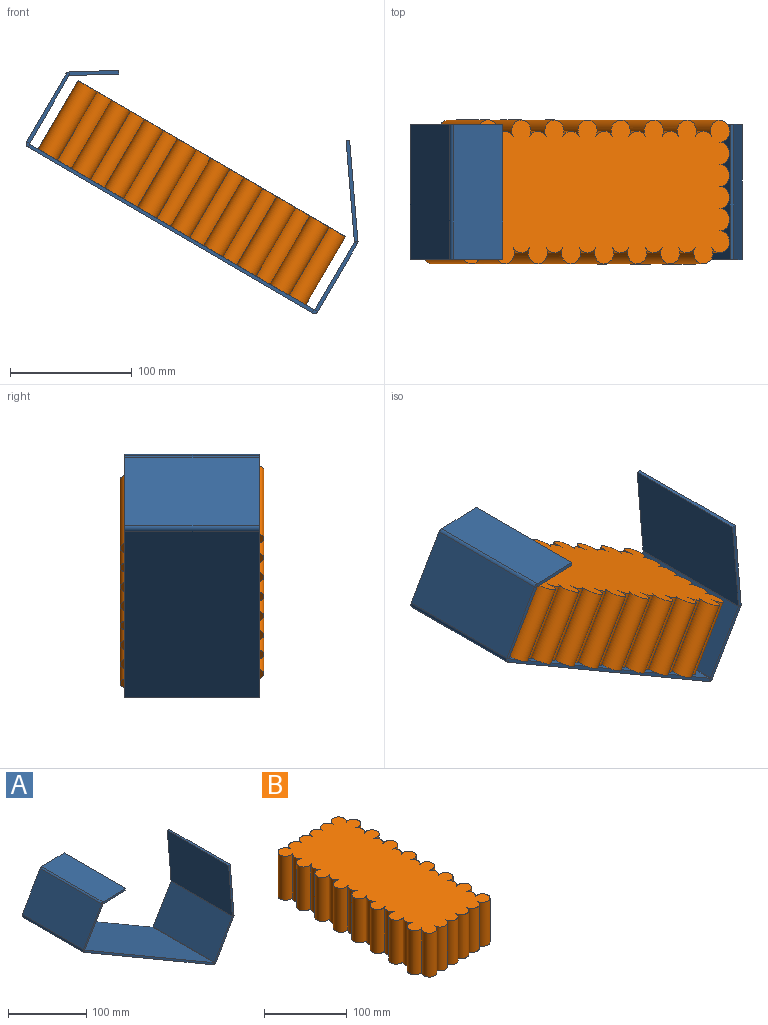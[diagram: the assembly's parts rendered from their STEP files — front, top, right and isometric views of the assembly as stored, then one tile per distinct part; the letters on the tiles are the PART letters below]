
ASSEMBLY  parts=2 mates=1
PART A: 38 faces, bbox 273x111x200 mm
  f0: plane 235.12x138.91mm, normal (0,-1,0), area 811.4mm2, adj f2,f3,f18,f35
  f1: plane 235.12x138.91mm, normal (0,1,0), area 811.4mm2, adj f2,f3,f17,f34
  f2: plane 233.6x136.32mm, normal (-0.5,0,-0.86), area 30022.3mm2, adj f0,f1,f19,f36
  f3: plane 233.6x136.32mm, normal (0.5,0,0.86), area 30022.3mm2, adj f0,f1,f20,f37
  f4: plane 40.59x4.22mm, normal (0,-1,0), area 121.5mm2, adj f5,f7,f8,f14
  f5: plane 111x3mm, normal (1,0,0.03), area 333mm2, adj f4,f6,f7,f8
  f6: plane 40.59x4.22mm, normal (0,1,0), area 121.5mm2, adj f5,f7,f8,f13
  f7: plane 111x40.5mm, normal (-0.03,0,1), area 4497.1mm2, adj f4,f5,f6,f15
  f8: plane 111x40.5mm, normal (0.03,0,-1), area 4497.1mm2, adj f4,f5,f6,f16
  f9: plane 56.98x34.96mm, normal (0,-1,0), area 192.7mm2, adj f11,f12,f14,f18
  f10: plane 56.98x34.96mm, normal (0,1,0), area 192.7mm2, adj f11,f12,f13,f17
  f11: plane 111x55.47mm, normal (-0.86,0,0.5), area 7128.7mm2, adj f9,f10,f15,f19
  f12: plane 111x55.47mm, normal (0.86,0,-0.5), area 7128.7mm2, adj f9,f10,f16,f20
  f13: plane 3.25x3.01mm, normal (0,1,0), area 6.1mm2, adj f6,f10,f15,f16
  f14: plane 3.25x3.01mm, normal (0,-1,0), area 6.1mm2, adj f4,f9,f15,f16
  f15: cylinder r=3.5mm len=111mm, axis (0,1,0), area 393.3mm2, adj f7,f11,f13,f14
  f16: cylinder r=0.5mm len=111mm, axis (0,1,0), area 56.2mm2, adj f8,f12,f13,f14
  f17: plane 4.79x3.25mm, normal (0,1,0), area 9.4mm2, adj f1,f10,f19,f20
  f18: plane 4.79x3.25mm, normal (0,-1,0), area 9.4mm2, adj f0,f9,f19,f20
  f19: cylinder r=3.5mm len=111mm, axis (0,1,0), area 610.3mm2, adj f2,f11,f17,f18
  f20: cylinder r=0.5mm len=111mm, axis (0,1,0), area 87.2mm2, adj f3,f12,f17,f18
  f21: plane 83.18x9.86mm, normal (0,-1,0), area 249.6mm2, adj f23,f24,f25,f31
  f22: plane 83.18x9.86mm, normal (0,1,0), area 249.6mm2, adj f23,f24,f25,f30
  f23: plane 111x2.99mm, normal (-0.08,0,1), area 333mm2, adj f21,f22,f24,f25
  f24: plane 111x82.93mm, normal (1,0,0.08), area 9236.9mm2, adj f21,f22,f23,f32
  f25: plane 111x82.93mm, normal (-1,0,-0.08), area 9236.9mm2, adj f21,f22,f23,f33
  f26: plane 57.08x35.02mm, normal (0,-1,0), area 193mm2, adj f28,f29,f31,f35
  f27: plane 57.08x35.02mm, normal (0,1,0), area 193mm2, adj f28,f29,f30,f34
  f28: plane 111x55.57mm, normal (0.86,0,-0.5), area 7142mm2, adj f26,f27,f32,f36
  f29: plane 111x55.57mm, normal (-0.86,0,0.5), area 7142mm2, adj f26,f27,f33,f37
  f30: plane 3.07x2.05mm, normal (0,1,0), area 3.7mm2, adj f22,f27,f32,f33
  f31: plane 3.07x2.05mm, normal (0,-1,0), area 3.7mm2, adj f21,f26,f32,f33
  f32: cylinder r=3.5mm len=111mm, axis (0,1,0), area 237.3mm2, adj f24,f28,f30,f31
  f33: cylinder r=0.5mm len=111mm, axis (0,1,0), area 33.9mm2, adj f25,f29,f30,f31
  f34: plane 4.79x3.25mm, normal (0,1,0), area 9.4mm2, adj f1,f27,f36,f37
  f35: plane 4.79x3.25mm, normal (0,-1,0), area 9.4mm2, adj f0,f26,f36,f37
  f36: cylinder r=3.5mm len=111mm, axis (0,1,0), area 610.3mm2, adj f2,f28,f34,f35
  f37: cylinder r=0.5mm len=111mm, axis (0,1,0), area 87.2mm2, adj f3,f29,f34,f35
PART B: 42 faces, bbox 118.3x254.6x65 mm
  f0: cylinder r=9.1mm len=65mm, axis (0,0,-1), area 2477.7mm2, adj f1,f39,f40,f41
  f1: cylinder r=9.1mm len=65mm, axis (0,0,-1), area 1858.3mm2, adj f0,f2,f40,f41
  f2: cylinder r=9.1mm len=65mm, axis (0,0,-1), area 1858.3mm2, adj f1,f3,f40,f41
  f3: cylinder r=9.1mm len=65mm, axis (0,0,-1), area 1858.3mm2, adj f2,f4,f40,f41
  f4: cylinder r=9.1mm len=65mm, axis (0,0,-1), area 1858.3mm2, adj f3,f5,f40,f41
  f5: cylinder r=9.1mm len=65mm, axis (0,0,-1), area 3097.1mm2, adj f4,f6,f40,f41
  f6: cylinder r=9.1mm len=65mm, axis (0,0,-1), area 1235.5mm2, adj f5,f7,f40,f41
  f7: cylinder r=9.1mm len=65mm, axis (0,0,-1), area 2474.4mm2, adj f6,f8,f40,f41
  f8: cylinder r=9.1mm len=65mm, axis (0,0,-1), area 1235.5mm2, adj f7,f9,f40,f41
  f9: cylinder r=9.1mm len=65mm, axis (0,0,-1), area 2474.4mm2, adj f8,f10,f40,f41
  f10: cylinder r=9.1mm len=65mm, axis (0,0,-1), area 1235.5mm2, adj f9,f11,f40,f41
  f11: cylinder r=9.1mm len=65mm, axis (0,0,-1), area 2474.4mm2, adj f10,f12,f40,f41
  f12: cylinder r=9.1mm len=65mm, axis (0,0,-1), area 1235.5mm2, adj f11,f13,f40,f41
  f13: cylinder r=9.1mm len=65mm, axis (0,0,-1), area 2474.4mm2, adj f12,f14,f40,f41
  f14: cylinder r=9.1mm len=65mm, axis (0,0,-1), area 1235.5mm2, adj f13,f15,f40,f41
  f15: cylinder r=9.1mm len=65mm, axis (0,0,-1), area 2474.4mm2, adj f14,f16,f40,f41
  f16: cylinder r=9.1mm len=65mm, axis (0,0,-1), area 1235.5mm2, adj f15,f17,f40,f41
  f17: cylinder r=9.1mm len=65mm, axis (0,0,-1), area 2474.4mm2, adj f16,f18,f40,f41
  f18: cylinder r=9.1mm len=65mm, axis (0,0,-1), area 1235.5mm2, adj f17,f19,f40,f41
  f19: cylinder r=9.1mm len=65mm, axis (0,0,-1), area 2474.4mm2, adj f18,f20,f40,f41
  f20: cylinder r=9.1mm len=65mm, axis (0,0,-1), area 2477.7mm2, adj f19,f21,f40,f41
  f21: cylinder r=9.1mm len=65mm, axis (0,0,-1), area 1858.3mm2, adj f20,f22,f40,f41
  f22: cylinder r=9.1mm len=65mm, axis (0,0,-1), area 1858.3mm2, adj f21,f23,f40,f41
  f23: cylinder r=9.1mm len=65mm, axis (0,0,-1), area 1858.3mm2, adj f22,f24,f40,f41
  f24: cylinder r=9.1mm len=65mm, axis (0,0,-1), area 1858.3mm2, adj f23,f25,f40,f41
  f25: cylinder r=9.1mm len=65mm, axis (0,0,-1), area 3097.1mm2, adj f24,f26,f40,f41
  f26: cylinder r=9.1mm len=65mm, axis (0,0,-1), area 1235.5mm2, adj f25,f27,f40,f41
  f27: cylinder r=9.1mm len=65mm, axis (0,0,-1), area 2474.4mm2, adj f26,f28,f40,f41
  f28: cylinder r=9.1mm len=65mm, axis (0,0,-1), area 1235.5mm2, adj f27,f29,f40,f41
  f29: cylinder r=9.1mm len=65mm, axis (0,0,-1), area 2474.4mm2, adj f28,f30,f40,f41
  f30: cylinder r=9.1mm len=65mm, axis (0,0,-1), area 1235.5mm2, adj f29,f31,f40,f41
  f31: cylinder r=9.1mm len=65mm, axis (0,0,-1), area 2474.4mm2, adj f30,f32,f40,f41
  f32: cylinder r=9.1mm len=65mm, axis (0,0,-1), area 1235.5mm2, adj f31,f33,f40,f41
  f33: cylinder r=9.1mm len=65mm, axis (0,0,-1), area 2474.4mm2, adj f32,f34,f40,f41
  f34: cylinder r=9.1mm len=65mm, axis (0,0,-1), area 1235.5mm2, adj f33,f35,f40,f41
  f35: cylinder r=9.1mm len=65mm, axis (0,0,-1), area 2474.4mm2, adj f34,f36,f40,f41
  f36: cylinder r=9.1mm len=65mm, axis (0,0,-1), area 1235.5mm2, adj f35,f37,f40,f41
  f37: cylinder r=9.1mm len=65mm, axis (0,0,-1), area 2474.4mm2, adj f36,f38,f40,f41
  f38: cylinder r=9.1mm len=65mm, axis (0,0,-1), area 1235.5mm2, adj f37,f39,f40,f41
  f39: cylinder r=9.1mm len=65mm, axis (0,0,-1), area 2474.4mm2, adj f0,f38,f40,f41
  f40: plane 254.62x118.3mm, normal (0,0,1), area 26977.7mm2, adj f0,f1,f2,f3,f4,f5,f6,f7
  f41: plane 254.62x118.3mm, normal (0,0,-1), area 26977.7mm2, adj f0,f1,f2,f3,f4,f5,f6,f7
PLACE A t=(-85.99,-74.01,33.6)mm
PLACE B rot(axis=(0.25,0.25,0.93),93.9deg) t=(-122.29,-170.46,54.78)mm
MATE fastened B.f41 <-> A.f3  axis (-0.5,0,-0.86) through (-224.39,-129.51,114.36)mm
